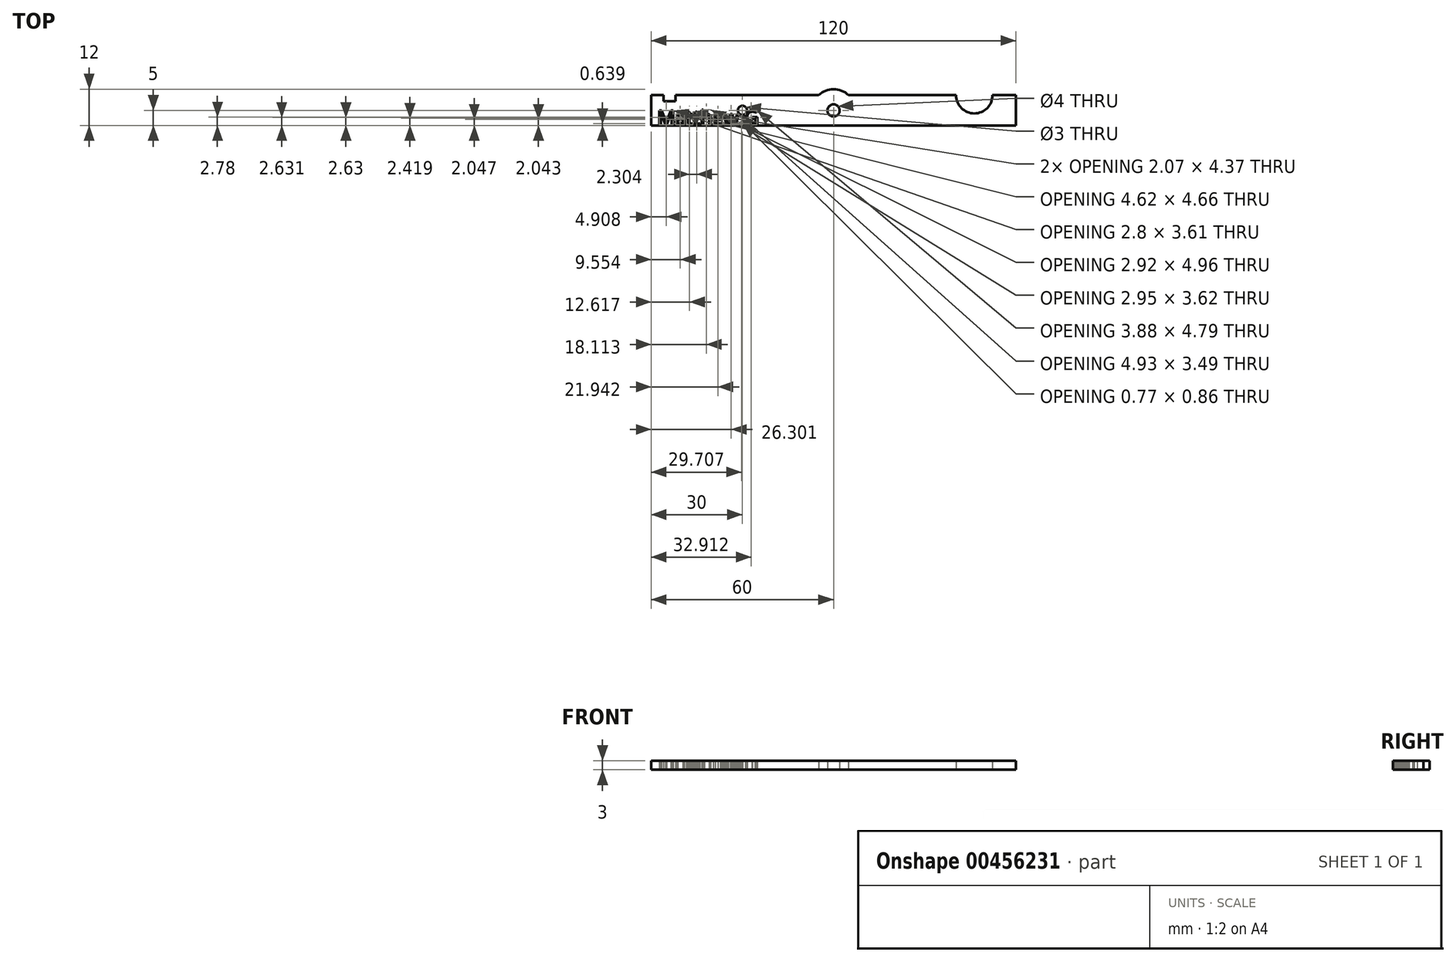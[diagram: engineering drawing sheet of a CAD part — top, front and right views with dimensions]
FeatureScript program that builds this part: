
annotation { "Feature Type Name" : "Feature", "Feature Type Description" : "" }
export const myFeature = defineFeature(function(context is Context, id is Id, definition is map)
    precondition{}
    {
        {
            var Q0;
            Q0=qCreatedBy(makeId("Top.planeOp"),FACE);
            var sketch = newSketch(context, id + "F0", { "sketchPlane" : qUnion([Q0])});
            skLineSegment(sketch, "E0.bottom", {"start": v(-60, 5) * mm, "end": v(60, 5) * mm});
            skLineSegment(sketch, "E0.top", {"start": v(-60, -5) * mm, "end": v(60, -5) * mm});
            skLineSegment(sketch, "E0.left", {"start": v(-60, 5) * mm, "end": v(-60, -5) * mm});
            skLineSegment(sketch, "E0.right", {"start": v(60, 5) * mm, "end": v(60, -5) * mm});
            skPoint(sketch, "E0.middle", {"position": v(0, 0) * mm});
            skLineSegment(sketch, "E1.bottom", {"start": v(-52, 5) * mm, "end": v(-56, 5) * mm});
            skLineSegment(sketch, "E1.top", {"start": v(-52, 3) * mm, "end": v(-56, 3) * mm});
            skLineSegment(sketch, "E1.left", {"start": v(-52, 5) * mm, "end": v(-52, 3) * mm});
            skLineSegment(sketch, "E1.right", {"start": v(-56, 5) * mm, "end": v(-56, 3) * mm});
            skPoint(sketch, "E1.middle", {"position": v(-54, 4) * mm});
            skCircle(sketch, "E2", {"center": v(0, 0) * mm, "radius": 2 * mm});
            skCircle(sketch, "E3", {"center": v(0, 0) * mm, "radius": 7 * mm});
            skCircle(sketch, "E4", {"center": v(-30, 0) * mm, "radius": 1.5 * mm});
            skCircle(sketch, "E5", {"center": v(46.3, 5) * mm, "radius": 6 * mm});
            skSolve(sketch);
        }
        {
            var Q0;
            {var subQ0=sQuery(id+"F0.wireOp",EDGE,"E0.right");Q0=makeQuery(id+"F0.imprint","IMPRINT",FACE,{"disambiguationData":[TD([[makeQuery(id+"F0.imprint","IMPRINT",EDGE,{"derivedFrom":subQ0}),-1.0]])]});}
            var Q1;
            Q1=makeQuery(id+"F0.imprint","IMPRINT",FACE,{"disambiguationData":[TD([[makeQuery(id+"F0.imprint","IMPRINT",EDGE,{"derivedFrom":sQuery(id+"F0.wireOp",EDGE,"E2")}),-1.0]])]});
            var Q2;
            {var subQ0=sQuery(id+"F0.wireOp",EDGE,"E3");var subQ1=sQuery(id+"F0.wireOp",EDGE,"E0.bottom");var subQ2=makeQuery(id+"F0.imprint","INTERSECT",VERTEX,{"disambiguationData":[OD(0.0)],"derivedFrom":[subQ1,subQ0]});Q2=makeQuery(id+"F0.imprint","IMPRINT",FACE,{"disambiguationData":[TD([[makeQuery(id+"F0.imprint","IMPRINT",EDGE,{"disambiguationData":[TD([[subQ2,-1.0]])],"derivedFrom":subQ1}),1.0]])]});}
            var Q3;
            {var subQ0=sQuery(id+"F0.wireOp",EDGE,"E3");var subQ1=sQuery(id+"F0.wireOp",EDGE,"E0.top");var subQ2=makeQuery(id+"F0.imprint","INTERSECT",VERTEX,{"disambiguationData":[OD(0.0)],"derivedFrom":[subQ1,subQ0]});Q3=makeQuery(id+"F0.imprint","IMPRINT",FACE,{"disambiguationData":[TD([[makeQuery(id+"F0.imprint","IMPRINT",EDGE,{"disambiguationData":[TD([[subQ2,-1.0]])],"derivedFrom":subQ1}),-1.0]])]});}
            var Q4;
            {var subQ0=sQuery(id+"F0.wireOp",EDGE,"E0.left");Q4=makeQuery(id+"F0.imprint","IMPRINT",FACE,{"disambiguationData":[TD([[makeQuery(id+"F0.imprint","IMPRINT",EDGE,{"derivedFrom":subQ0}),1.0]])]});}
            extrude(context, id + "F1", {"entities" : qUnion([Q0, Q1, Q2, Q3, Q4]), "depth" : 3 * mm});
        }
        {
            var Q0;
            Q0=qCreatedBy(makeId("Top.planeOp"),FACE);
            var sketch = newSketch(context, id + "F2", { "sketchPlane" : qUnion([Q0])});
            skText(sketch, "E6", { "text": "Matthew.G", "fontName": "OpenSans-Regular.ttf"});
            const initialGuessF2  = {"E6": [-0.05804, -0.0047, 1, 0, 0.0047]};
            skSetInitialGuess(sketch, initialGuessF2);
            skSolve(sketch);
        }
        {
            var Q0;
            Q0=makeQuery(id+"F2.imprint","IMPRINT",FACE,{"disambiguationData":[TD([[makeQuery(id+"F2.imprint","IMPRINT",EDGE,{"derivedFrom":sQuery(id+"F2.wireOp",EDGE,"E6.sketch_text.stroke-143")}),-1.0]])]});
            var Q1;
            Q1=makeQuery(id+"F2.imprint","IMPRINT",FACE,{"disambiguationData":[TD([[makeQuery(id+"F2.imprint","IMPRINT",EDGE,{"derivedFrom":sQuery(id+"F2.wireOp",EDGE,"E6.sketch_text.stroke-120")}),-1.0]])]});
            var Q2;
            Q2=makeQuery(id+"F2.imprint","IMPRINT",FACE,{"disambiguationData":[TD([[makeQuery(id+"F2.imprint","IMPRINT",EDGE,{"derivedFrom":sQuery(id+"F2.wireOp",EDGE,"E6.sketch_text.stroke-151")}),-1.0]])]});
            var Q3;
            Q3=makeQuery(id+"F2.imprint","IMPRINT",FACE,{"disambiguationData":[TD([[makeQuery(id+"F2.imprint","IMPRINT",EDGE,{"derivedFrom":sQuery(id+"F2.wireOp",EDGE,"E6.sketch_text.stroke-101")}),-1.0]])]});
            var Q4;
            Q4=makeQuery(id+"F2.imprint","IMPRINT",FACE,{"disambiguationData":[TD([[makeQuery(id+"F2.imprint","IMPRINT",EDGE,{"derivedFrom":sQuery(id+"F2.wireOp",EDGE,"E6.sketch_text.stroke-83")}),-1.0]])]});
            var Q5;
            Q5=makeQuery(id+"F2.imprint","IMPRINT",FACE,{"disambiguationData":[TD([[makeQuery(id+"F2.imprint","IMPRINT",EDGE,{"derivedFrom":sQuery(id+"F2.wireOp",EDGE,"E6.sketch_text.stroke-64")}),-1.0]])]});
            var Q6;
            Q6=makeQuery(id+"F2.imprint","IMPRINT",FACE,{"disambiguationData":[TD([[makeQuery(id+"F2.imprint","IMPRINT",EDGE,{"derivedFrom":sQuery(id+"F2.wireOp",EDGE,"E6.sketch_text.stroke-45")}),-1.0]])]});
            var Q7;
            Q7=makeQuery(id+"F2.imprint","IMPRINT",FACE,{"disambiguationData":[TD([[makeQuery(id+"F2.imprint","IMPRINT",EDGE,{"derivedFrom":sQuery(id+"F2.wireOp",EDGE,"E6.sketch_text.stroke-18")}),-1.0]])]});
            var Q8;
            Q8=makeQuery(id+"F2.imprint","IMPRINT",FACE,{"disambiguationData":[TD([[makeQuery(id+"F2.imprint","IMPRINT",EDGE,{"derivedFrom":sQuery(id+"F2.wireOp",EDGE,"E6.sketch_text.stroke-0")}),-1.0]])]});
            extrude(context, id + "F3", {"entities" : qUnion([Q0, Q1, Q2, Q3, Q4, Q5, Q6, Q7, Q8]), "operationType" : NewBodyOperationType.REMOVE, "depth" : 25 * mm});
        }
    });
